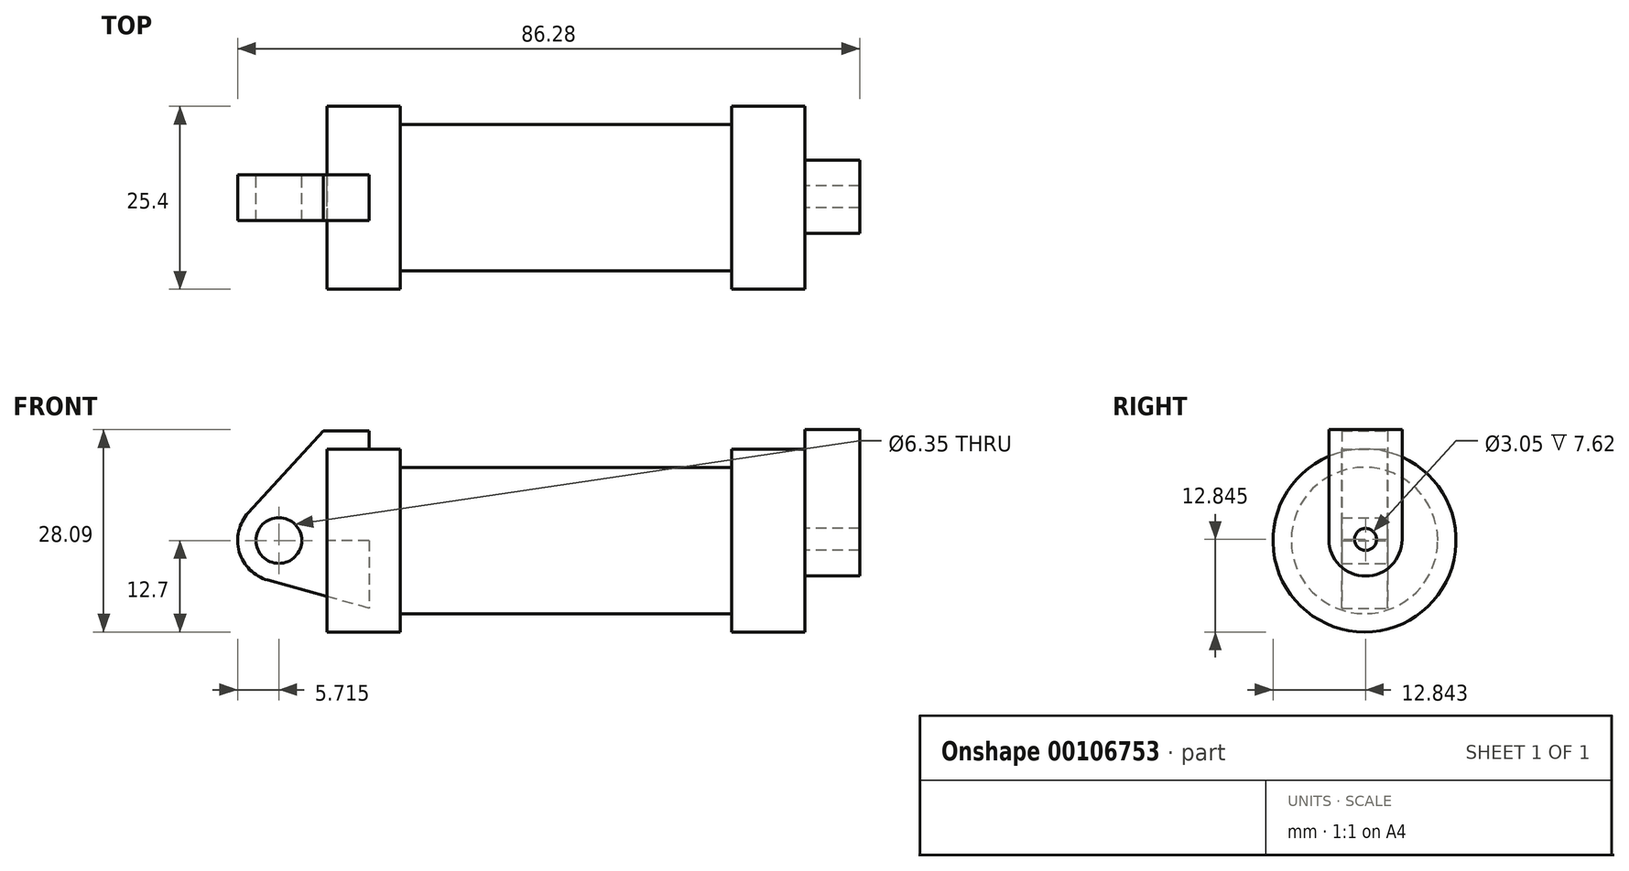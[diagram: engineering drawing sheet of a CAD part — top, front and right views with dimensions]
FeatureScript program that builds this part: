
annotation { "Feature Type Name" : "Feature", "Feature Type Description" : "" }
export const myFeature = defineFeature(function(context is Context, id is Id, definition is map)
    precondition{}
    {
        {
            var Q0;
            Q0=qCreatedBy(makeId("Front.planeOp"),FACE);
            var sketch = newSketch(context, id + "F0", { "sketchPlane" : qUnion([Q0])});
            skLineSegment(sketch, "E0", {"start": v(0, 0) * mm, "end": v(0, 12.7) * mm});
            skLineSegment(sketch, "E1", {"start": v(0, 12.7) * mm, "end": v(10.16, 12.7) * mm});
            skLineSegment(sketch, "E2", {"start": v(10.16, 12.7) * mm, "end": v(10.16, 10.16) * mm});
            skLineSegment(sketch, "E3", {"start": v(10.16, 10.16) * mm, "end": v(56.13, 10.16) * mm});
            skLineSegment(sketch, "E4", {"start": v(56.13, 10.16) * mm, "end": v(56.13, 12.7) * mm});
            skLineSegment(sketch, "E5", {"start": v(56.13, 12.7) * mm, "end": v(66.3, 12.7) * mm});
            skLineSegment(sketch, "E6", {"start": v(66.3, 12.7) * mm, "end": v(66.3, 0) * mm});
            skLineSegment(sketch, "E7", {"start": v(66.3, 0) * mm, "end": v(0, 0) * mm});
            skLineSegment(sketch, "E8", {"start": v(5.84, 15.24) * mm, "end": v(-0.5, 15.24) * mm});
            skLineSegment(sketch, "E9", {"start": v(-0.5, 15.24) * mm, "end": v(-10.88, 3.85) * mm});
            skLineSegment(sketch, "E10", {"start": v(0, 0) * mm, "end": v(-6.65, 0) * mm});
            skCircle(sketch, "E11", {"center": v(-6.65, 0) * mm, "radius": 5.72 * mm});
            skCircle(sketch, "E12", {"center": v(-6.65, 0) * mm, "radius": 3.18 * mm});
            skLineSegment(sketch, "E13", {"start": v(5.84, 15.24) * mm, "end": v(5.84, -9.4) * mm});
            skLineSegment(sketch, "E14", {"start": v(5.84, -9.4) * mm, "end": v(-8.18, -5.5) * mm});
            skSolve(sketch);
        }
        {
            var Q0;
            {var subQ0=sQuery(id+"F0.wireOp",EDGE,"E0");Q0=makeQuery(id+"F0.imprint","IMPRINT",FACE,{"disambiguationData":[TD([[makeQuery(id+"F0.imprint","IMPRINT",EDGE,{"derivedFrom":subQ0}),-1.0]])]});}
            var Q1;
            {var subQ0=sQuery(id+"F0.wireOp",EDGE,"E2");Q1=makeQuery(id+"F0.imprint","IMPRINT",FACE,{"disambiguationData":[TD([[makeQuery(id+"F0.imprint","IMPRINT",EDGE,{"derivedFrom":subQ0}),-1.0]])]});}
            var Q2;
            Q2=sQuery(id+"F0.wireOp",EDGE,"E7");
            revolve(context, id + "F1", {"entities" : qUnion([Q0, Q1]), "axis" : qUnion([Q2]), "revolveType" : RevolveType.FULL});
        }
        {
            var Q0;
            {var subQ3=sQuery(id+"F0.wireOp",EDGE,"E0");Q0=makeQuery(id+"F0.imprint","IMPRINT",FACE,{"disambiguationData":[TD([[makeQuery(id+"F0.imprint","IMPRINT",EDGE,{"derivedFrom":subQ3}),1.0]])]});}
            var Q1;
            {var subQ0=sQuery(id+"F0.wireOp",EDGE,"E14");Q1=makeQuery(id+"F0.imprint","IMPRINT",FACE,{"disambiguationData":[TD([[makeQuery(id+"F0.imprint","IMPRINT",EDGE,{"derivedFrom":subQ0}),-1.0]])]});}
            var Q2;
            {var subQ4=sQuery(id+"F0.wireOp",EDGE,"E12");Q2=makeQuery(id+"F0.imprint","IMPRINT",FACE,{"disambiguationData":[TD([[makeQuery(id+"F0.imprint","IMPRINT",EDGE,{"derivedFrom":subQ4}),-1.0]])]});}
            extrude(context, id + "F2", {"entities" : qUnion([Q0, Q1, Q2]), "endBound" : BoundingType.SYMMETRIC, "depth" : 6.35 * mm});
        }
        {
            var Q0;
            Q0=makeQuery(id+"F1.opRevolve","SWEPT_FACE",FACE,{"disambiguationData":[OSD([sQuery(id+"F0.wireOp",EDGE,"E6")])]});
            var sketch = newSketch(context, id + "F3", { "sketchPlane" : qUnion([Q0])});
            skCircle(sketch, "E15", {"center": v(0.14, 0.15) * mm, "radius": 5.08 * mm});
            skCircle(sketch, "E16", {"center": v(0.14, 0.15) * mm, "radius": 1.52 * mm});
            skLineSegment(sketch, "E17", {"start": v(-4.94, 0.15) * mm, "end": v(-4.94, 15.39) * mm});
            skLineSegment(sketch, "E18", {"start": v(5.22, 0.15) * mm, "end": v(5.22, 15.39) * mm});
            skLineSegment(sketch, "E19", {"start": v(-4.94, 15.39) * mm, "end": v(5.22, 15.39) * mm});
            skSolve(sketch);
        }
        {
            var Q0;
            {var subQ0=sQuery(id+"F3.wireOp",EDGE,"E19");Q0=makeQuery(id+"F3.imprint","IMPRINT",FACE,{"disambiguationData":[TD([[makeQuery(id+"F3.imprint","IMPRINT",EDGE,{"derivedFrom":subQ0}),-1.0]])]});}
            var Q1;
            {var subQ0=sQuery(id+"F3.wireOp",EDGE,"E17");var subQ1=sQuery(id+"F3.wireOp",EDGE,"E15");var subQ2=makeQuery(id+"F3.imprint","INTERSECT",VERTEX,{"derivedFrom":[subQ1,subQ0]});Q1=makeQuery(id+"F3.imprint","IMPRINT",FACE,{"disambiguationData":[TD([[makeQuery(id+"F3.imprint","IMPRINT",EDGE,{"disambiguationData":[TD([[subQ2,1.0]])],"derivedFrom":subQ1}),-1.0]])]});}
            var Q2;
            Q2=makeQuery(id+"F3.imprint","IMPRINT",FACE,{"disambiguationData":[TD([[makeQuery(id+"F3.imprint","IMPRINT",EDGE,{"derivedFrom":sQuery(id+"F3.wireOp",EDGE,"E16")}),-1.0]])]});
            extrude(context, id + "F4", {"entities" : qUnion([Q0, Q1, Q2]), "operationType" : NewBodyOperationType.ADD, "depth" : 7.62 * mm});
        }
    });
